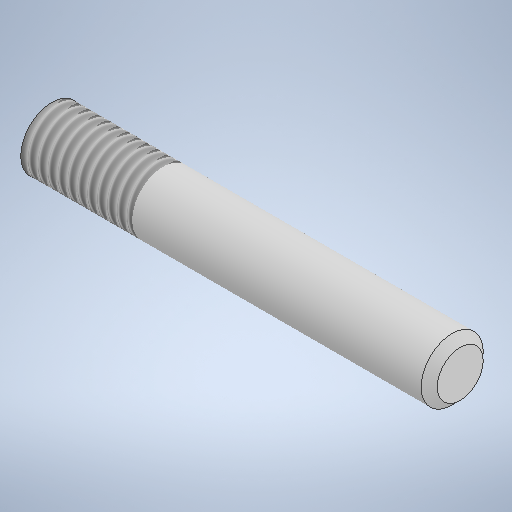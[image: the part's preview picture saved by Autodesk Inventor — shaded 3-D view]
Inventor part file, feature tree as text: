
AUTODESK INVENTOR PART (.ipt)
format: ipt  version: 2025.1 (Build 291241000, 241)  size: 267,776 bytes
history: native  units: mm
features: revolve x1, thread x1, chamfer x1, sketch x1
ambient origin geometry x8: Origin, YZ Plane, XZ Plane, XY Plane, X Axis, Y Axis, Z Axis, Center Point
bodies: Solid1 (feature_tree)
feature tree (4):
  revolve  "Revolution1"  [1 undecoded]
  thread  "Thread1"  [1 undecoded]
  chamfer  "Chamfer1"  Distance=9.0mm
  sketch  "Sketch1"  dims[d0=33.0mm d1=5.0mm d2=90.0deg d3=9.0mm d4=0.0mm d5=0.65mm d6=2.0mm d7=45.0deg]
note: 2 required parameter values undecoded (feature->parameter linkage not recoverable at this tier; creation-order binding heuristic only, values carry confidence <= 0.55)